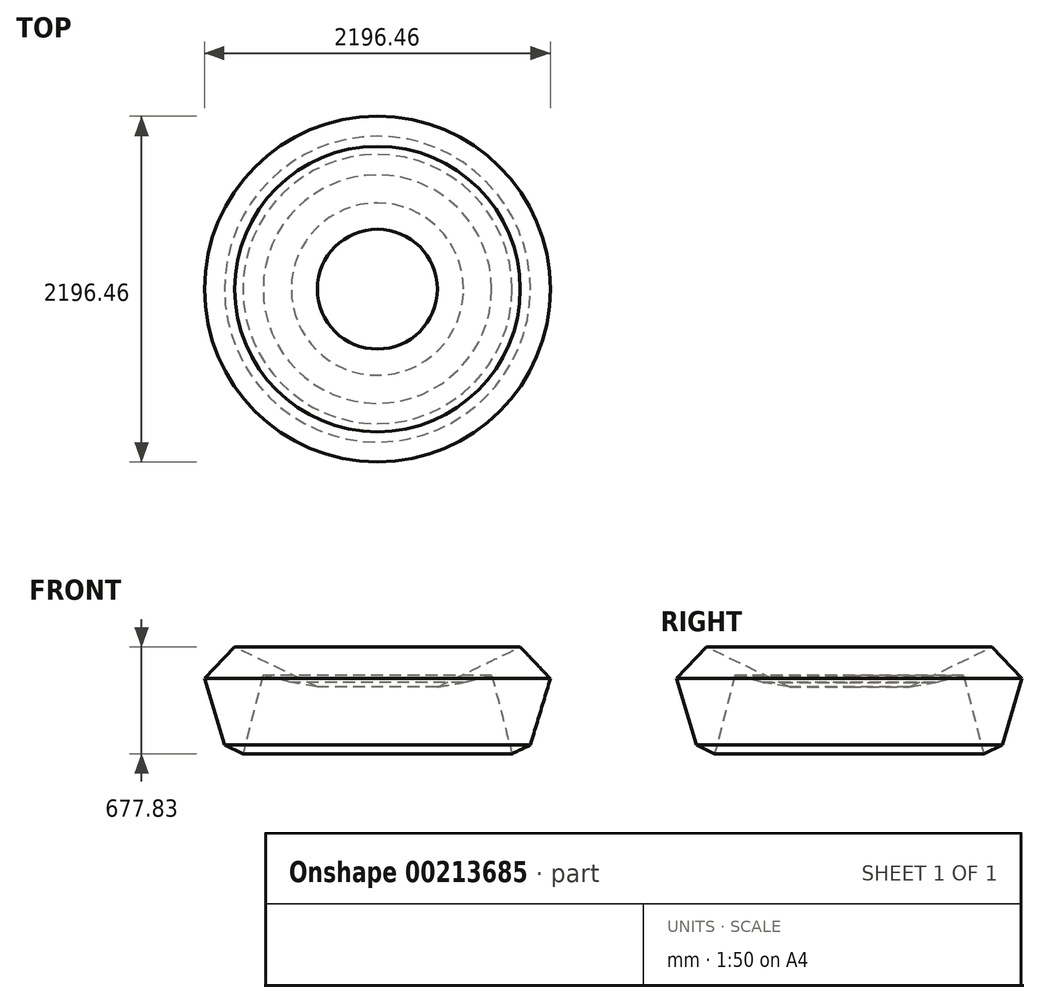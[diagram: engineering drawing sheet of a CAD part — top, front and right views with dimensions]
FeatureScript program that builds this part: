
annotation { "Feature Type Name" : "Feature", "Feature Type Description" : "" }
export const myFeature = defineFeature(function(context is Context, id is Id, definition is map)
    precondition{}
    {
        {
            var Q0;
            Q0=qCreatedBy(makeId("Front.planeOp"),FACE);
            var sketch = newSketch(context, id + "F0", { "sketchPlane" : qUnion([Q0])});
            skLineSegment(sketch, "E0", {"start": v(-906.82, 200.46) * mm, "end": v(-1098.23, 0) * mm});
            skLineSegment(sketch, "E1", {"start": v(-1098.23, 0) * mm, "end": v(-971.26, -422.7) * mm});
            skLineSegment(sketch, "E2", {"start": v(-971.26, -422.7) * mm, "end": v(-854.8, -477.37) * mm});
            skLineSegment(sketch, "E3", {"start": v(-854.8, -477.37) * mm, "end": v(-725.73, 21.3) * mm});
            skLineSegment(sketch, "E4", {"start": v(-725.73, 21.3) * mm, "end": v(-547.17, -24.92) * mm});
            skLineSegment(sketch, "E5", {"start": v(-547.17, -24.92) * mm, "end": v(-381, -53.23) * mm});
            skLineSegment(sketch, "E6", {"start": v(-381, -53.23) * mm, "end": v(-906.82, 200.46) * mm});
            skLineSegment(sketch, "E7", {"start": v(0, 0) * mm, "end": v(0, -355.38) * mm, "construction": true});
            skSolve(sketch);
        }
        {
            var Q0;
            Q0 = qSketchRegion(id + "F0", true);
            var Q1;
            Q1=sQuery(id+"F0.wireOp",EDGE,"E7");
            revolve(context, id + "F1", {"entities" : qUnion([Q0]), "axis" : qUnion([Q1]), "revolveType" : RevolveType.FULL});
        }
    });
